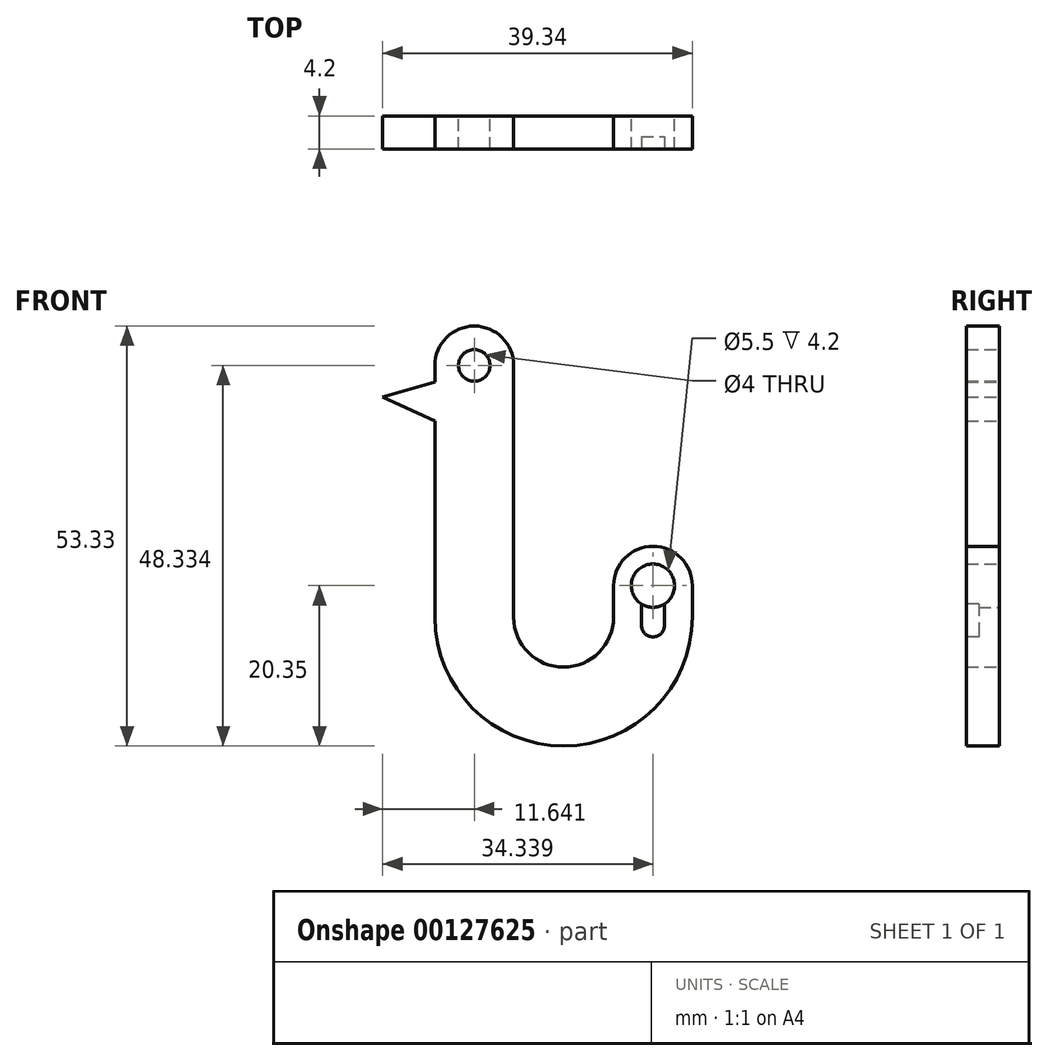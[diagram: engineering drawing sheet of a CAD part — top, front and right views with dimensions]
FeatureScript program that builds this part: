
annotation { "Feature Type Name" : "Feature", "Feature Type Description" : "" }
export const myFeature = defineFeature(function(context is Context, id is Id, definition is map)
    precondition{}
    {
        {
            assignVariable(context, id + "F0", {"name" : "thickness", "anyValue" : 4.2 * mm});
        }
        {
            var Q0;
            Q0=qCreatedBy(makeId("Front.planeOp"),FACE);
            var sketch = newSketch(context, id + "F1", { "sketchPlane" : qUnion([Q0])});
            skCircle(sketch, "E0", {"center": v(0, 0) * mm, "radius": 40 * mm, "construction": true});
            skLineSegment(sketch, "E1.bottom", {"start": v(-6.35, 27.98) * mm, "end": v(-16.35, 27.98) * mm, "construction": true});
            skLineSegment(sketch, "E1.left", {"start": v(-6.35, 27.98) * mm, "end": v(-6.35, -4) * mm});
            skLineSegment(sketch, "E1.right", {"start": v(-16.35, 27.98) * mm, "end": v(-16.35, 25.88) * mm});
            skLineSegment(sketch, "E2.top", {"start": v(-6.35, -4) * mm, "end": v(6.35, -4) * mm, "construction": true});
            skLineSegment(sketch, "E3.top", {"start": v(11.35, 5) * mm, "end": v(11.35, 5) * mm});
            skLineSegment(sketch, "E3.right", {"start": v(6.35, -4) * mm, "end": v(6.35, 0) * mm});
            skArc(sketch, "E4", {"start": v(-6.35, -4) * mm, "mid": v(0, -10.35) * mm, "end": v(6.35, -4) * mm});
            skArc(sketch, "E5", {"start": v(-6.35, 27.98) * mm, "mid": v(-11.35, 32.98) * mm, "end": v(-16.35, 27.98) * mm});
            skArc(sketch, "E6", {"start": v(-16.35, -4) * mm, "mid": v(0, -20.35) * mm, "end": v(16.35, -4) * mm});
            skLineSegment(sketch, "E7", {"start": v(16.35, -4) * mm, "end": v(16.35, 0) * mm});
            skCircle(sketch, "E8", {"center": v(-11.35, 27.98) * mm, "radius": 2 * mm});
            skLineSegment(sketch, "E9", {"start": v(-16.35, 25.88) * mm, "end": v(-22.99, 23.98) * mm});
            skLineSegment(sketch, "E10", {"start": v(-22.99, 23.98) * mm, "end": v(-16.35, 20.94) * mm});
            skLineSegment(sketch, "E11", {"start": v(-3.77, 23.98) * mm, "end": v(-22.99, 23.98) * mm, "construction": true});
            skPoint(sketch, "E12.visualSharp", {"position": v(6.35, 5) * mm});
            skPoint(sketch, "E13.visualSharp", {"position": v(16.35, 5) * mm});
            skCircle(sketch, "E14", {"center": v(11.35, 0) * mm, "radius": 2.75 * mm});
            skLineSegment(sketch, "E15.trimOffspring", {"start": v(-16.35, 20.94) * mm, "end": v(-16.35, -4) * mm});
            skArc(sketch, "E16", {"start": v(6.35, 0) * mm, "mid": v(11.35, 5) * mm, "end": v(16.35, 0) * mm});
            skSolve(sketch);
        }
        {
            var Q0;
            Q0=makeQuery(id+"F1.imprint","IMPRINT",FACE,{"disambiguationData":[TD([[makeQuery(id+"F1.imprint","IMPRINT",EDGE,{"derivedFrom":sQuery(id+"F1.wireOp",EDGE,"E1.left")}),-1.0]])]});
            extrude(context, id + "F2", {"entities" : qUnion([Q0]), "depth" : getVariable(context, 'thickness')});
        }
        {
            var Q0;
            Q0=makeQuery(id+"F2.opExtrude","CAP_FACE",FACE,{"disambiguationData":[OSD([sQuery(id+"F1.wireOp",EDGE,"E1.left"),sQuery(id+"F1.wireOp",EDGE,"E1.right"),sQuery(id+"F1.wireOp",EDGE,"E3.right"),sQuery(id+"F1.wireOp",EDGE,"E4"),sQuery(id+"F1.wireOp",EDGE,"E5"),sQuery(id+"F1.wireOp",EDGE,"E6"),sQuery(id+"F1.wireOp",EDGE,"E7"),sQuery(id+"F1.wireOp",EDGE,"E8"),sQuery(id+"F1.wireOp",EDGE,"E9"),sQuery(id+"F1.wireOp",EDGE,"E10"),sQuery(id+"F1.wireOp",EDGE,"E12.filletArc"),sQuery(id+"F1.wireOp",EDGE,"E13.filletArc"),sQuery(id+"F1.wireOp",EDGE,"E14"),sQuery(id+"F1.wireOp",EDGE,"E15.trimOffspring")])],"isStart":false});
            var sketch = newSketch(context, id + "F3", { "sketchPlane" : qUnion([Q0])});
            skArc(sketch, "E17", {"start": v(12.8, -2.34) * mm, "mid": v(11.35, 2.75) * mm, "end": v(9.9, -2.34) * mm});
            skArc(sketch, "E18", {"start": v(9.9, -5.05) * mm, "mid": v(11.35, -6.5) * mm, "end": v(12.8, -5.05) * mm});
            skLineSegment(sketch, "E19", {"start": v(9.9, -2.34) * mm, "end": v(9.9, -5.05) * mm});
            skLineSegment(sketch, "E20", {"start": v(12.8, -2.34) * mm, "end": v(12.8, -5.05) * mm});
            skLineSegment(sketch, "E21", {"start": v(11.35, 2.75) * mm, "end": v(11.35, -8.27) * mm, "construction": true});
            skPoint(sketch, "E22", {"position": v(11.35, -6.5) * mm});
            skSolve(sketch);
        }
        {
            var Q0;
            Q0=makeQuery(id+"F3.imprint","IMPRINT",FACE,{"disambiguationData":[TD([[makeQuery(id+"F3.imprint","IMPRINT",EDGE,{"derivedFrom":sQuery(id+"F3.wireOp",EDGE,"E17")}),1.0]])]});
            var Q1;
            Q1=makeQuery(id+"F3.imprint","IMPRINT",FACE,{"disambiguationData":[TD([[makeQuery(id+"F3.imprint","IMPRINT",EDGE,{"derivedFrom":sQuery(id+"F3.wireOp",EDGE,"E18")}),1.0]])]});
            extrude(context, id + "F4", {"entities" : qUnion([Q0, Q1]), "operationType" : NewBodyOperationType.REMOVE, "oppositeDirection" : true, "depth" : getVariable(context, 'thickness') - 2.6 * mm});
        }
    });
